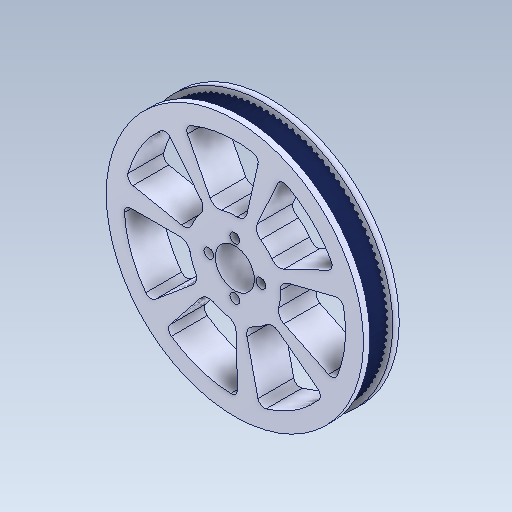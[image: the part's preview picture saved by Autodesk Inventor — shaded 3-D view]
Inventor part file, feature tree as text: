
AUTODESK INVENTOR PART (.ipt)
format: ipt  version: 2020 (Build 240168000, 168)  size: 3,919,872 bytes
history: native  units: mm
features: extrude x6, sketch x6, reference x6, other x4, fillet x3, pattern_circular x2, projected_geometry x2, thicken_offset x1, chamfer x1
ambient origin geometry x8: Origin, YZ Plane, XZ Plane, XY Plane, X Axis, Y Axis, Z Axis, Center Point
bodies: Solid1 (feature_tree)
feature tree (31):
  thicken_offset  "Thicken1"
  extrude  "Extrusion1"  Depth=1.0mm
  extrude  "Extrusion2"  Depth=10.0mm TaperAngle=0.0deg
  extrude  "Extrusion3"  Depth=2.0mm
  extrude  "Extrusion4"  Depth=2.0mm TaperAngle=0.0deg
  extrude  "Extrusion5"  Depth=2.0mm TaperAngle=0.0deg
  chamfer  "Chamfer1"  Distance=2.0mm Angle=45.0deg
  extrude  "Extrusion6"  Depth=7.0mm
  pattern_circular  "Circular Pattern1"  [2 undecoded]
  fillet  "Fillet2"  Radius=28.0mm
  fillet  "Fillet3"  Radius=68.0mm
  pattern_circular  "Circular Pattern2"  [2 undecoded]
  fillet  "Fillet4"  Radius=70.0mm
  sketch  "Sketch1"  dims[d0=1.0mm d1=1.0mm]
  sketch  "Sketch2"  dims[d2=79.0mm d3=10.0mm d4=0.0mm]
  sketch  "Sketch3"  dims[d5=2.0mm d6=0.0mm d7=12.0mm]
  reference  "Reference1"
  sketch  "Sketch4"  dims[d8=2.0mm d9=0.0mm d10=20.0mm d11=0.0mm]
  reference  "Reference2"
  reference  "Reference3"
  reference  "Reference4"
  reference  "Reference5"
  sketch  "Sketch5"  dims[d12=24.0mm d13=2.0mm d14=0.0mm d16=2.0mm d17=2.0mm d18=45.0deg]
  projected_geometry  "Projected Loop1"
  reference  "Reference6"
  sketch  "Sketch6"  dims[d19=34.0mm d20=34.0mm d21=6.981317mm d22=28.0mm d23=68.0mm d24=12.0mm d25=0.0mm d26=70.0mm d27=360.0deg d29=3.0mm d30=2.0mm d31=70.0mm d32=360.0deg d34=7.0mm]
  projected_geometry  "Projected Loop2"
  other  "Boss-Extrude3"
  parser-record x1  (decoder bookkeeping rows leaked as tree rows — omitted from the tree; the rows remain in map.json)
  other  "belt_reducer_1.iam"
  other  "flange_6mm:1"
note: 4 required parameter values undecoded (feature->parameter linkage not recoverable at this tier; creation-order binding heuristic only, values carry confidence <= 0.55)
note: 1 file-system path scrubbed to <path> (originals preserved in map.json)
